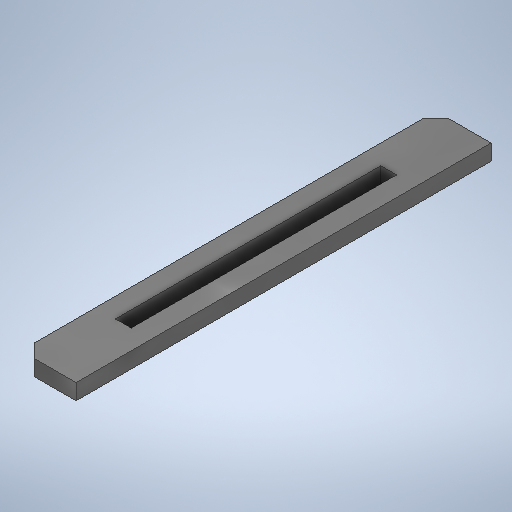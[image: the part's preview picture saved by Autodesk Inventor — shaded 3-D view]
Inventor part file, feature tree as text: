
AUTODESK INVENTOR PART (.ipt)
format: ipt  version: 2025 (Build 290162000, 162)  size: 280,064 bytes
history: native  units: in
note: dims shown in document units (in); Inventor stores cm internally (conversion verified against a paired STEP export)
features: extrude x3, sketch x3
ambient origin geometry x8: Origin, YZ Plane, XZ Plane, XY Plane, X Axis, Y Axis, Z Axis, Center Point
bodies: Solid1 (feature_tree)
feature tree (6):
  extrude  "Extrusion1"  Depth=0.0236in TaperAngle=0.0deg
  extrude  "Extrusion2"  Depth=0.3976in
  extrude  "Extrusion3"  Depth=0.0413in
  sketch  "Sketch1"  dims[d0=0.622in d1=0.0236in d2=0.0in]
  sketch  "Sketch2"  dims[d3=0.0236in d4=0.3976in]
  sketch  "Sketch3"  dims[d5=0.0in d6=0.0in d7=0.0413in d8=0.0413in d9=0.0197in d10=0.0197in d11=0.0197in d12=0.0197in d13=0.0in d14=0.0in d15=0.311in]
